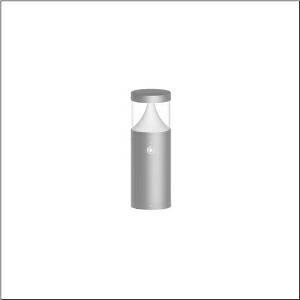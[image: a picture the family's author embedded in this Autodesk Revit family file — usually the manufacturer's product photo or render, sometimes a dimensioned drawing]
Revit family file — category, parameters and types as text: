
# Revit family: cl_31_poller_40_sensor_5cl424803
name_source: partatom
category: Lighting Fixtures
units: mm (PartAtom-declared; Revit-internal decimal feet)

## family parameters
Cut with Voids When Loaded = No
Host = Face
Light Source = No
Part Type = Normal
Room Calculation Point = No
Round Connector Dimension = Use Diameter
Shared = No

## types (1)
- --- (1 x LED, 800 lm, 7.2 W, 3000K)
    Apparent Load = 7 VA
    CIE Flux Codes = 19 66 88 92 100
    Color Rendering = 80
    Color Temperature = 3000K
    Default Elevation = 1800 mm
    Description = CL 31 Bollard 40 Sensor, bollard luminaire, primary light control with lens, of PC, primary optical cover: cover panel, of PC, transparent, secondary light control with reflector, of PC, primary light characteristic: asymmetric, LED, rated luminous flux: 800lm, luminous efficacy: 110lm/W, light colour: 830, colour temperature: 3000K, control gear: ECG DALI, with terminal, 5-pole, max. 2.5mm², mains connection: 220..240V, AC, 50/60Hz, rated input power: 7.2W, luminaire housing, of aluminium, powder-coated, Siteco® metallic grey, diameter: 170mm, height: 400mm, PIR sensor, protection rating (complete): IP65, insulation class (complete): insulation class I (protective earthing), certification: CE, ENEC, impact resistance: IK08, permissible operating ambient temperature for outdoor applications: -20..+50°C, packaging unit: 1 piece
    Height = 200 mm  [stored 0.656168 ft]
    Lamp = 1 x LED
    Lamp Light Flux = 800 lm
    Lamp Power = 7.2 W
    Lamp count = 1
    Length = 170 mm  [stored 0.557743 ft]
    Luminous efficacy = 111 lm/W
    Manufacturer = Siteco
    ModVariant = No
    Model = 5CL424803
    Mounting Place = Floor
    Mounting Type = Freestanding
    Number of Poles = 1
    OnlyDefault = Yes
    Power Factor = 1
    Product Name = CL 31 Poller 40 Sensor
    Product group = bollard luminaire | freestanding
    ProductGroupID = 1303
    Protection Class = Protection class I
    Protection Degree = IP 65
    RLX_Detail_Level = 1
    RlxData = <blob elided: 62825 chars, md5=3feac0e1>
    Socket = socket
    Standby Power = 0 W
    System Light Flux = 800 lm
    System Power = 7 W
    Type Comments = factory setting: luminous flux: 100 % | dim-lin: 254 | 182 mA
    Type Image = l_1006905.jpg
    URL = http://relux.com
    VarID = @adj_116935
    Voltage = 0 V
    Weight = 0.00 kg
    Width = 0 mm  [stored 0 ft]

note: [stored X ft] marks values corroborated as IEEE doubles in the binary element streams (Revit-internal decimal feet)

## geometry (parser evidence)
native form markers: Blend x4, Sweep x14
no freeform markers — native parametric forms only
